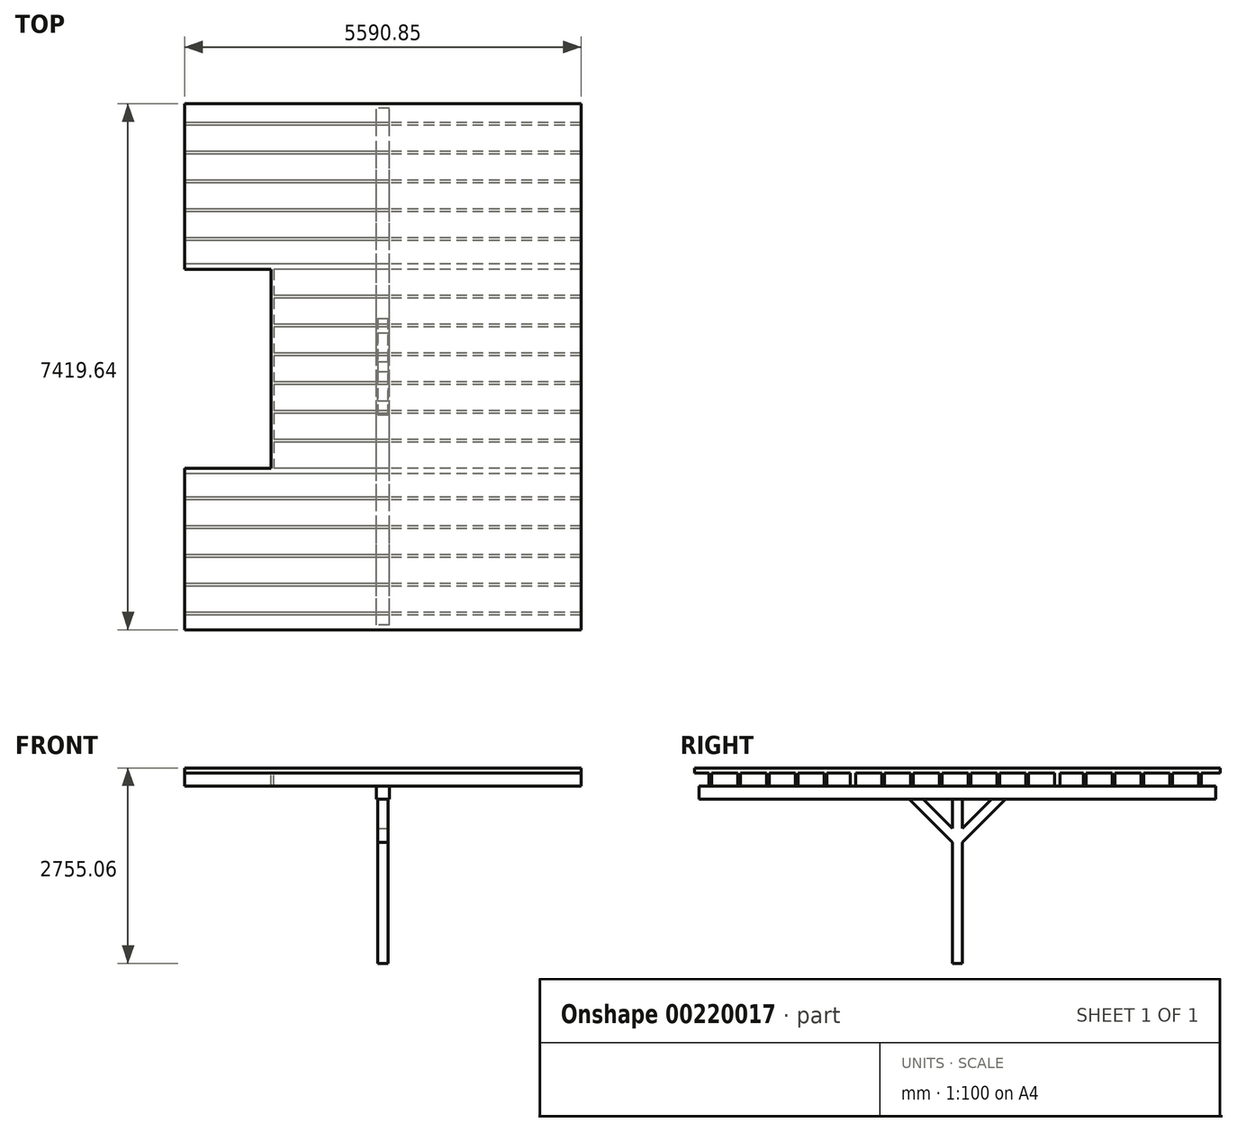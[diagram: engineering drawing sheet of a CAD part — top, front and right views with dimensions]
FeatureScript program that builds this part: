
annotation { "Feature Type Name" : "Feature", "Feature Type Description" : "" }
export const myFeature = defineFeature(function(context is Context, id is Id, definition is map)
    precondition{}
    {
        {
            var Q0;
            Q0=qCreatedBy(makeId("Top.planeOp"),FACE);
            var sketch = newSketch(context, id + "F0", { "sketchPlane" : qUnion([Q0])});
            skLineSegment(sketch, "E0.bottom", {"start": v(-4.2, 0) * mm, "end": v(5863.2, 0) * mm});
            skLineSegment(sketch, "E0.top", {"start": v(-4.2, -7696.2) * mm, "end": v(5863.2, -7696.2) * mm});
            skLineSegment(sketch, "E0.left", {"start": v(-4.2, 0) * mm, "end": v(-4.2, -7696.2) * mm});
            skLineSegment(sketch, "E0.right", {"start": v(5863.2, 0) * mm, "end": v(5863.2, -7696.2) * mm});
            skSolve(sketch);
        }
        {
            var Q0;
            Q0=makeQuery(id+"F0.imprint","IMPRINT",FACE,{"disambiguationData":[TD([[makeQuery(id+"F0.imprint","IMPRINT",EDGE,{"derivedFrom":sQuery(id+"F0.wireOp",EDGE,"E0.bottom")}),-1.0]])]});
            extrude(context, id + "F1", {"entities" : qUnion([Q0]), "depth" : 69.14 * mm});
        }
        {
            var Q0;
            Q0=makeQuery(id+"F1.opExtrude","CAP_FACE",FACE,{"disambiguationData":[OSD([sQuery(id+"F0.wireOp",EDGE,"E0.bottom"),sQuery(id+"F0.wireOp",EDGE,"E0.top"),sQuery(id+"F0.wireOp",EDGE,"E0.left"),sQuery(id+"F0.wireOp",EDGE,"E0.right")])],"isStart":true});
            var sketch = newSketch(context, id + "F2", { "sketchPlane" : qUnion([Q0])});
            skLineSegment(sketch, "E1.0", {"start": v(33.9, 7658.1) * mm, "end": v(5825.1, 7658.1) * mm});
            skLineSegment(sketch, "E1.1", {"start": v(33.9, 38.1) * mm, "end": v(33.9, 7658.1) * mm});
            skLineSegment(sketch, "E1.2", {"start": v(33.9, 38.1) * mm, "end": v(5825.1, 38.1) * mm});
            skLineSegment(sketch, "E1.3", {"start": v(5825.1, 38.1) * mm, "end": v(5825.1, 7658.1) * mm});
            skSolve(sketch);
        }
        {
            var Q0;
            Q0=makeQuery(id+"F2.imprint","IMPRINT",FACE,{"disambiguationData":[TD([[makeQuery(id+"F2.imprint","IMPRINT",EDGE,{"derivedFrom":sQuery(id+"F2.wireOp",EDGE,"E1.0")}),1.0]])]});
            extrude(context, id + "F3", {"entities" : qUnion([Q0]), "operationType" : NewBodyOperationType.ADD, "depth" : 184.15 * mm});
        }
        {
            var Q0;
            Q0=qCreatedBy(makeId("Right.planeOp"),FACE);
            var sketch = newSketch(context, id + "F4", { "sketchPlane" : qUnion([Q0])});
            skLineSegment(sketch, "E2.bottom", {"start": v(-406.4, 0) * mm, "end": v(-444.5, 0) * mm});
            skLineSegment(sketch, "E2.top", {"start": v(-406.4, -184.15) * mm, "end": v(-444.5, -184.15) * mm});
            skLineSegment(sketch, "E2.left", {"start": v(-406.4, 0) * mm, "end": v(-406.4, -184.15) * mm});
            skLineSegment(sketch, "E2.right", {"start": v(-444.5, 0) * mm, "end": v(-444.5, -184.15) * mm});
            skLineSegment(sketch, "E3.1.0.0", {"start": v(-812.8, 0) * mm, "end": v(-812.8, -184.15) * mm});
            skLineSegment(sketch, "E3.1.0.1", {"start": v(-850.9, 0) * mm, "end": v(-850.9, -184.15) * mm});
            skLineSegment(sketch, "E3.1.0.2", {"start": v(-812.8, 0) * mm, "end": v(-850.9, 0) * mm});
            skLineSegment(sketch, "E3.1.0.3", {"start": v(-812.8, -184.15) * mm, "end": v(-850.9, -184.15) * mm});
            skLineSegment(sketch, "E3.2.0.0", {"start": v(-1219.2, 0) * mm, "end": v(-1219.2, -184.15) * mm});
            skLineSegment(sketch, "E3.2.0.1", {"start": v(-1257.3, 0) * mm, "end": v(-1257.3, -184.15) * mm});
            skLineSegment(sketch, "E3.2.0.2", {"start": v(-1219.2, 0) * mm, "end": v(-1257.3, 0) * mm});
            skLineSegment(sketch, "E3.2.0.3", {"start": v(-1219.2, -184.15) * mm, "end": v(-1257.3, -184.15) * mm});
            skLineSegment(sketch, "E3.3.0.0", {"start": v(-1625.6, 0) * mm, "end": v(-1625.6, -184.15) * mm});
            skLineSegment(sketch, "E3.3.0.1", {"start": v(-1663.7, 0) * mm, "end": v(-1663.7, -184.15) * mm});
            skLineSegment(sketch, "E3.3.0.2", {"start": v(-1625.6, 0) * mm, "end": v(-1663.7, 0) * mm});
            skLineSegment(sketch, "E3.3.0.3", {"start": v(-1625.6, -184.15) * mm, "end": v(-1663.7, -184.15) * mm});
            skLineSegment(sketch, "E3.4.0.0", {"start": v(-2032, 0) * mm, "end": v(-2032, -184.15) * mm});
            skLineSegment(sketch, "E3.4.0.1", {"start": v(-2070.1, 0) * mm, "end": v(-2070.1, -184.15) * mm});
            skLineSegment(sketch, "E3.4.0.2", {"start": v(-2032, 0) * mm, "end": v(-2070.1, 0) * mm});
            skLineSegment(sketch, "E3.4.0.3", {"start": v(-2032, -184.15) * mm, "end": v(-2070.1, -184.15) * mm});
            skLineSegment(sketch, "E3.5.0.0", {"start": v(-2438.4, 0) * mm, "end": v(-2438.4, -184.15) * mm});
            skLineSegment(sketch, "E3.5.0.1", {"start": v(-2476.5, 0) * mm, "end": v(-2476.5, -184.15) * mm});
            skLineSegment(sketch, "E3.5.0.2", {"start": v(-2438.4, 0) * mm, "end": v(-2476.5, 0) * mm});
            skLineSegment(sketch, "E3.5.0.3", {"start": v(-2438.4, -184.15) * mm, "end": v(-2476.5, -184.15) * mm});
            skLineSegment(sketch, "E3.6.0.0", {"start": v(-2844.8, 0) * mm, "end": v(-2844.8, -184.15) * mm});
            skLineSegment(sketch, "E3.6.0.1", {"start": v(-2882.9, 0) * mm, "end": v(-2882.9, -184.15) * mm});
            skLineSegment(sketch, "E3.6.0.2", {"start": v(-2844.8, 0) * mm, "end": v(-2882.9, 0) * mm});
            skLineSegment(sketch, "E3.6.0.3", {"start": v(-2844.8, -184.15) * mm, "end": v(-2882.9, -184.15) * mm});
            skLineSegment(sketch, "E3.7.0.0", {"start": v(-3251.2, 0) * mm, "end": v(-3251.2, -184.15) * mm});
            skLineSegment(sketch, "E3.7.0.1", {"start": v(-3289.3, 0) * mm, "end": v(-3289.3, -184.15) * mm});
            skLineSegment(sketch, "E3.7.0.2", {"start": v(-3251.2, 0) * mm, "end": v(-3289.3, 0) * mm});
            skLineSegment(sketch, "E3.7.0.3", {"start": v(-3251.2, -184.15) * mm, "end": v(-3289.3, -184.15) * mm});
            skLineSegment(sketch, "E3.8.0.0", {"start": v(-3657.6, 0) * mm, "end": v(-3657.6, -184.15) * mm});
            skLineSegment(sketch, "E3.8.0.1", {"start": v(-3695.7, 0) * mm, "end": v(-3695.7, -184.15) * mm});
            skLineSegment(sketch, "E3.8.0.2", {"start": v(-3657.6, 0) * mm, "end": v(-3695.7, 0) * mm});
            skLineSegment(sketch, "E3.8.0.3", {"start": v(-3657.6, -184.15) * mm, "end": v(-3695.7, -184.15) * mm});
            skLineSegment(sketch, "E3.9.0.0", {"start": v(-4064, 0) * mm, "end": v(-4064, -184.15) * mm});
            skLineSegment(sketch, "E3.9.0.1", {"start": v(-4102.1, 0) * mm, "end": v(-4102.1, -184.15) * mm});
            skLineSegment(sketch, "E3.9.0.2", {"start": v(-4064, 0) * mm, "end": v(-4102.1, 0) * mm});
            skLineSegment(sketch, "E3.9.0.3", {"start": v(-4064, -184.15) * mm, "end": v(-4102.1, -184.15) * mm});
            skLineSegment(sketch, "E3.10.0.0", {"start": v(-4470.4, 0) * mm, "end": v(-4470.4, -184.15) * mm});
            skLineSegment(sketch, "E3.10.0.1", {"start": v(-4508.5, 0) * mm, "end": v(-4508.5, -184.15) * mm});
            skLineSegment(sketch, "E3.10.0.2", {"start": v(-4470.4, 0) * mm, "end": v(-4508.5, 0) * mm});
            skLineSegment(sketch, "E3.10.0.3", {"start": v(-4470.4, -184.15) * mm, "end": v(-4508.5, -184.15) * mm});
            skLineSegment(sketch, "E3.11.0.0", {"start": v(-4876.8, 0) * mm, "end": v(-4876.8, -184.15) * mm});
            skLineSegment(sketch, "E3.11.0.1", {"start": v(-4914.9, 0) * mm, "end": v(-4914.9, -184.15) * mm});
            skLineSegment(sketch, "E3.11.0.2", {"start": v(-4876.8, 0) * mm, "end": v(-4914.9, 0) * mm});
            skLineSegment(sketch, "E3.11.0.3", {"start": v(-4876.8, -184.15) * mm, "end": v(-4914.9, -184.15) * mm});
            skLineSegment(sketch, "E3.12.0.0", {"start": v(-5283.2, 0) * mm, "end": v(-5283.2, -184.15) * mm});
            skLineSegment(sketch, "E3.12.0.1", {"start": v(-5321.3, 0) * mm, "end": v(-5321.3, -184.15) * mm});
            skLineSegment(sketch, "E3.12.0.2", {"start": v(-5283.2, 0) * mm, "end": v(-5321.3, 0) * mm});
            skLineSegment(sketch, "E3.12.0.3", {"start": v(-5283.2, -184.15) * mm, "end": v(-5321.3, -184.15) * mm});
            skLineSegment(sketch, "E3.13.0.0", {"start": v(-5689.6, 0) * mm, "end": v(-5689.6, -184.15) * mm});
            skLineSegment(sketch, "E3.13.0.1", {"start": v(-5727.7, 0) * mm, "end": v(-5727.7, -184.15) * mm});
            skLineSegment(sketch, "E3.13.0.2", {"start": v(-5689.6, 0) * mm, "end": v(-5727.7, 0) * mm});
            skLineSegment(sketch, "E3.13.0.3", {"start": v(-5689.6, -184.15) * mm, "end": v(-5727.7, -184.15) * mm});
            skLineSegment(sketch, "E3.14.0.0", {"start": v(-6096, 0) * mm, "end": v(-6096, -184.15) * mm});
            skLineSegment(sketch, "E3.14.0.1", {"start": v(-6134.1, 0) * mm, "end": v(-6134.1, -184.15) * mm});
            skLineSegment(sketch, "E3.14.0.2", {"start": v(-6096, 0) * mm, "end": v(-6134.1, 0) * mm});
            skLineSegment(sketch, "E3.14.0.3", {"start": v(-6096, -184.15) * mm, "end": v(-6134.1, -184.15) * mm});
            skLineSegment(sketch, "E3.15.0.0", {"start": v(-6502.4, 0) * mm, "end": v(-6502.4, -184.15) * mm});
            skLineSegment(sketch, "E3.15.0.1", {"start": v(-6540.5, 0) * mm, "end": v(-6540.5, -184.15) * mm});
            skLineSegment(sketch, "E3.15.0.2", {"start": v(-6502.4, 0) * mm, "end": v(-6540.5, 0) * mm});
            skLineSegment(sketch, "E3.15.0.3", {"start": v(-6502.4, -184.15) * mm, "end": v(-6540.5, -184.15) * mm});
            skLineSegment(sketch, "E3.16.0.0", {"start": v(-6908.8, 0) * mm, "end": v(-6908.8, -184.15) * mm});
            skLineSegment(sketch, "E3.16.0.1", {"start": v(-6946.9, 0) * mm, "end": v(-6946.9, -184.15) * mm});
            skLineSegment(sketch, "E3.16.0.2", {"start": v(-6908.8, 0) * mm, "end": v(-6946.9, 0) * mm});
            skLineSegment(sketch, "E3.16.0.3", {"start": v(-6908.8, -184.15) * mm, "end": v(-6946.9, -184.15) * mm});
            skLineSegment(sketch, "E3.direction1", {"start": v(-444.5, -184.15) * mm, "end": v(-850.9, -184.15) * mm, "construction": true});
            skLineSegment(sketch, "E4.0.17.0", {"start": v(-7315.2, 0) * mm, "end": v(-7315.2, -184.15) * mm});
            skLineSegment(sketch, "E4.3.17.0", {"start": v(-7353.3, 0) * mm, "end": v(-7353.3, -184.15) * mm});
            skLineSegment(sketch, "E4.6.17.0", {"start": v(-7315.2, 0) * mm, "end": v(-7353.3, 0) * mm});
            skLineSegment(sketch, "E4.9.17.0", {"start": v(-7315.2, -184.15) * mm, "end": v(-7353.3, -184.15) * mm});
            skSolve(sketch);
        }
        {
            var Q0;
            Q0=makeQuery(id+"F4.imprint","IMPRINT",FACE,{"disambiguationData":[TD([[makeQuery(id+"F4.imprint","IMPRINT",EDGE,{"derivedFrom":sQuery(id+"F4.wireOp",EDGE,"E2.bottom")}),1.0]])]});
            var Q1;
            Q1=makeQuery(id+"F4.imprint","IMPRINT",FACE,{"disambiguationData":[TD([[makeQuery(id+"F4.imprint","IMPRINT",EDGE,{"derivedFrom":sQuery(id+"F4.wireOp",EDGE,"E3.1.0.0")}),-1.0]])]});
            var Q2;
            Q2=makeQuery(id+"F4.imprint","IMPRINT",FACE,{"disambiguationData":[TD([[makeQuery(id+"F4.imprint","IMPRINT",EDGE,{"derivedFrom":sQuery(id+"F4.wireOp",EDGE,"E3.2.0.0")}),-1.0]])]});
            var Q3;
            Q3=makeQuery(id+"F4.imprint","IMPRINT",FACE,{"disambiguationData":[TD([[makeQuery(id+"F4.imprint","IMPRINT",EDGE,{"derivedFrom":sQuery(id+"F4.wireOp",EDGE,"E3.3.0.0")}),-1.0]])]});
            var Q4;
            Q4=makeQuery(id+"F4.imprint","IMPRINT",FACE,{"disambiguationData":[TD([[makeQuery(id+"F4.imprint","IMPRINT",EDGE,{"derivedFrom":sQuery(id+"F4.wireOp",EDGE,"E3.4.0.0")}),-1.0]])]});
            var Q5;
            Q5=makeQuery(id+"F4.imprint","IMPRINT",FACE,{"disambiguationData":[TD([[makeQuery(id+"F4.imprint","IMPRINT",EDGE,{"derivedFrom":sQuery(id+"F4.wireOp",EDGE,"E3.5.0.0")}),-1.0]])]});
            var Q6;
            Q6=makeQuery(id+"F4.imprint","IMPRINT",FACE,{"disambiguationData":[TD([[makeQuery(id+"F4.imprint","IMPRINT",EDGE,{"derivedFrom":sQuery(id+"F4.wireOp",EDGE,"E3.6.0.0")}),-1.0]])]});
            var Q7;
            Q7=makeQuery(id+"F4.imprint","IMPRINT",FACE,{"disambiguationData":[TD([[makeQuery(id+"F4.imprint","IMPRINT",EDGE,{"derivedFrom":sQuery(id+"F4.wireOp",EDGE,"E3.7.0.0")}),-1.0]])]});
            var Q8;
            Q8=makeQuery(id+"F4.imprint","IMPRINT",FACE,{"disambiguationData":[TD([[makeQuery(id+"F4.imprint","IMPRINT",EDGE,{"derivedFrom":sQuery(id+"F4.wireOp",EDGE,"E3.8.0.0")}),-1.0]])]});
            var Q9;
            Q9=makeQuery(id+"F4.imprint","IMPRINT",FACE,{"disambiguationData":[TD([[makeQuery(id+"F4.imprint","IMPRINT",EDGE,{"derivedFrom":sQuery(id+"F4.wireOp",EDGE,"E3.9.0.0")}),-1.0]])]});
            var Q10;
            Q10=makeQuery(id+"F4.imprint","IMPRINT",FACE,{"disambiguationData":[TD([[makeQuery(id+"F4.imprint","IMPRINT",EDGE,{"derivedFrom":sQuery(id+"F4.wireOp",EDGE,"E3.10.0.0")}),-1.0]])]});
            var Q11;
            Q11=makeQuery(id+"F4.imprint","IMPRINT",FACE,{"disambiguationData":[TD([[makeQuery(id+"F4.imprint","IMPRINT",EDGE,{"derivedFrom":sQuery(id+"F4.wireOp",EDGE,"E3.11.0.0")}),-1.0]])]});
            var Q12;
            Q12=makeQuery(id+"F4.imprint","IMPRINT",FACE,{"disambiguationData":[TD([[makeQuery(id+"F4.imprint","IMPRINT",EDGE,{"derivedFrom":sQuery(id+"F4.wireOp",EDGE,"E3.12.0.0")}),-1.0]])]});
            var Q13;
            Q13=makeQuery(id+"F4.imprint","IMPRINT",FACE,{"disambiguationData":[TD([[makeQuery(id+"F4.imprint","IMPRINT",EDGE,{"derivedFrom":sQuery(id+"F4.wireOp",EDGE,"E3.13.0.0")}),-1.0]])]});
            var Q14;
            Q14=makeQuery(id+"F4.imprint","IMPRINT",FACE,{"disambiguationData":[TD([[makeQuery(id+"F4.imprint","IMPRINT",EDGE,{"derivedFrom":sQuery(id+"F4.wireOp",EDGE,"E3.14.0.0")}),-1.0]])]});
            var Q15;
            Q15=makeQuery(id+"F4.imprint","IMPRINT",FACE,{"disambiguationData":[TD([[makeQuery(id+"F4.imprint","IMPRINT",EDGE,{"derivedFrom":sQuery(id+"F4.wireOp",EDGE,"E3.15.0.0")}),-1.0]])]});
            var Q16;
            Q16=makeQuery(id+"F4.imprint","IMPRINT",FACE,{"disambiguationData":[TD([[makeQuery(id+"F4.imprint","IMPRINT",EDGE,{"derivedFrom":sQuery(id+"F4.wireOp",EDGE,"E3.16.0.0")}),-1.0]])]});
            var Q17;
            Q17=makeQuery(id+"F4.imprint","IMPRINT",FACE,{"disambiguationData":[TD([[makeQuery(id+"F4.imprint","IMPRINT",EDGE,{"derivedFrom":sQuery(id+"F4.wireOp",EDGE,"E4.0.17.0")}),-1.0]])]});
            var Q18;
            Q18=makeQuery(id+"F1.opExtrude","SWEPT_FACE",FACE,{"disambiguationData":[OSD([sQuery(id+"F0.wireOp",EDGE,"E0.right")])]});
            extrude(context, id + "F5", {"entities" : qUnion([Q0, Q1, Q2, Q3, Q4, Q5, Q6, Q7, Q8, Q9, Q10, Q11, Q12, Q13, Q14, Q15, Q16, Q17]), "operationType" : NewBodyOperationType.ADD, "endBound" : BoundingType.UP_TO_SURFACE, "endBoundEntityFace" : qUnion([Q18]), "depth" : 25.4 * mm});
        }
        {
            var Q0;
            {var subQ0=sQuery(id+"F0.wireOp",EDGE,"E0.bottom");Q0=makeQuery(id+"F3.boolean.opBoolean","MERGE",FACE,{"derivedFrom":[makeQuery(id+"F1.opExtrude","SWEPT_FACE",FACE,{"disambiguationData":[OSD([subQ0])]}),makeQuery(id+"F3.opExtrude","SWEPT_FACE",FACE,{"disambiguationData":[OSD([subQ0])]})]});}
            cPlane(context, id + "F6", {"entities" : qUnion([Q0]), "cplaneType" : CPlaneType.OFFSET, "offset" : 203.2 * mm, "oppositeDirection" : true, "width" : 152.4 * mm, "height" : 152.4 * mm});
        }
        {
            var Q0;
            Q0=qCreatedBy(id+"F6.planeOp",FACE);
            var sketch = newSketch(context, id + "F7", { "sketchPlane" : qUnion([Q0])});
            skLineSegment(sketch, "E5.bottom", {"start": v(-3021.58, -184.15) * mm, "end": v(-2837.43, -184.15) * mm});
            skLineSegment(sketch, "E5.top", {"start": v(-3021.58, -368.3) * mm, "end": v(-2837.43, -368.3) * mm});
            skLineSegment(sketch, "E5.left", {"start": v(-3021.58, -184.15) * mm, "end": v(-3021.58, -368.3) * mm});
            skLineSegment(sketch, "E5.right", {"start": v(-2837.43, -184.15) * mm, "end": v(-2837.43, -368.3) * mm});
            skSolve(sketch);
        }
        {
            var Q0;
            Q0=makeQuery(id+"F7.imprint","IMPRINT",FACE,{"disambiguationData":[TD([[makeQuery(id+"F7.imprint","IMPRINT",EDGE,{"derivedFrom":sQuery(id+"F7.wireOp",EDGE,"E5.bottom")}),-1.0]])]});
            extrude(context, id + "F8", {"entities" : qUnion([Q0]), "operationType" : NewBodyOperationType.ADD, "oppositeDirection" : true, "depth" : 7289.8 * mm});
        }
        {
            var Q0;
            Q0=makeQuery(id+"F8.opExtrude","SWEPT_FACE",FACE,{"disambiguationData":[OSD([sQuery(id+"F7.wireOp",EDGE,"E5.top")])]});
            var sketch = newSketch(context, id + "F9", { "sketchPlane" : qUnion([Q0])});
            skLineSegment(sketch, "E6", {"start": v(2929.5, 7493) * mm, "end": v(2929.5, 203.2) * mm, "construction": true});
            skLineSegment(sketch, "E7", {"start": v(2837.43, 3848.1) * mm, "end": v(3021.58, 3848.1) * mm, "construction": true});
            skLineSegment(sketch, "E8.bottom", {"start": v(2999.36, 3778.25) * mm, "end": v(2859.66, 3778.25) * mm});
            skLineSegment(sketch, "E8.top", {"start": v(2999.36, 3917.95) * mm, "end": v(2859.66, 3917.95) * mm});
            skLineSegment(sketch, "E8.left", {"start": v(2999.36, 3778.25) * mm, "end": v(2999.36, 3917.95) * mm});
            skLineSegment(sketch, "E8.right", {"start": v(2859.66, 3778.25) * mm, "end": v(2859.66, 3917.95) * mm});
            skPoint(sketch, "E8.middle", {"position": v(2929.5, 3848.1) * mm});
            skSolve(sketch);
        }
        {
            var Q0;
            Q0=makeQuery(id+"F9.imprint","IMPRINT",FACE,{"disambiguationData":[TD([[makeQuery(id+"F9.imprint","IMPRINT",EDGE,{"derivedFrom":sQuery(id+"F9.wireOp",EDGE,"E8.bottom")}),-1.0]])]});
            extrude(context, id + "F10", {"entities" : qUnion([Q0]), "operationType" : NewBodyOperationType.ADD, "depth" : 2317.62 * mm});
        }
        {
            var Q0;
            Q0=makeQuery(id+"F10.opExtrude","SWEPT_FACE",FACE,{"disambiguationData":[OSD([sQuery(id+"F9.wireOp",EDGE,"E8.left")])]});
            var sketch = newSketch(context, id + "F11", { "sketchPlane" : qUnion([Q0])});
            skLineSegment(sketch, "E9", {"start": v(-4329.98, -368.3) * mm, "end": v(-3917.95, -780.33) * mm});
            skLineSegment(sketch, "E10", {"start": v(-3917.95, -780.33) * mm, "end": v(-3917.95, -977.9) * mm});
            skLineSegment(sketch, "E11", {"start": v(-3917.95, -977.9) * mm, "end": v(-4527.55, -368.3) * mm});
            skLineSegment(sketch, "E12", {"start": v(-4527.55, -368.3) * mm, "end": v(-4329.98, -368.3) * mm});
            skLineSegment(sketch, "E13", {"start": v(-3848.1, -1904.76) * mm, "end": v(-3848.1, -2685.92) * mm, "construction": true});
            skLineSegment(sketch, "E14.MirrorCS", {"start": v(-3168.65, -368.3) * mm, "end": v(-3366.22, -368.3) * mm});
            skLineSegment(sketch, "E15.MirrorCS", {"start": v(-3778.25, -977.9) * mm, "end": v(-3168.65, -368.3) * mm});
            skLineSegment(sketch, "E16.MirrorCS", {"start": v(-3366.22, -368.3) * mm, "end": v(-3778.25, -780.33) * mm});
            skLineSegment(sketch, "E17.MirrorCS", {"start": v(-3778.25, -780.33) * mm, "end": v(-3778.25, -977.9) * mm});
            skSolve(sketch);
        }
        {
            var Q0;
            Q0=makeQuery(id+"F11.imprint","IMPRINT",FACE,{"disambiguationData":[TD([[makeQuery(id+"F11.imprint","IMPRINT",EDGE,{"derivedFrom":sQuery(id+"F11.wireOp",EDGE,"E9")}),-1.0]])]});
            var Q1;
            Q1=makeQuery(id+"F11.imprint","IMPRINT",FACE,{"disambiguationData":[TD([[makeQuery(id+"F11.imprint","IMPRINT",EDGE,{"derivedFrom":sQuery(id+"F11.wireOp",EDGE,"E14.MirrorCS")}),1.0]])]});
            var Q2;
            Q2=makeQuery(id+"F11.imprint","IMPRINT",FACE,{"disambiguationData":[TD([[makeQuery(id+"F11.imprint","IMPRINT",EDGE,{"derivedFrom":sQuery(id+"F11.wireOp",EDGE,"E14.MirrorCS")}),-1.0]])]});
            var Q3;
            Q3=makeQuery(id+"F10.opExtrude","SWEPT_FACE",FACE,{"disambiguationData":[OSD([sQuery(id+"F9.wireOp",EDGE,"E8.right")])]});
            extrude(context, id + "F12", {"entities" : qUnion([Q0, Q1, Q2]), "operationType" : NewBodyOperationType.ADD, "endBound" : BoundingType.UP_TO_SURFACE, "oppositeDirection" : true, "endBoundEntityFace" : qUnion([Q3]), "depth" : 25.4 * mm});
        }
        {
            var Q0;
            Q0=makeQuery(id+"F1.opExtrude","CAP_FACE",FACE,{"disambiguationData":[OSD([sQuery(id+"F0.wireOp",EDGE,"E0.bottom"),sQuery(id+"F0.wireOp",EDGE,"E0.top"),sQuery(id+"F0.wireOp",EDGE,"E0.left"),sQuery(id+"F0.wireOp",EDGE,"E0.right")])],"isStart":false});
            var sketch = newSketch(context, id + "F13", { "sketchPlane" : qUnion([Q0])});
            skLineSegment(sketch, "E18.0", {"start": v(134.08, -138.28) * mm, "end": v(5724.93, -138.28) * mm});
            skLineSegment(sketch, "E18.1", {"start": v(134.08, -138.28) * mm, "end": v(134.08, -7557.92) * mm});
            skLineSegment(sketch, "E18.2", {"start": v(134.08, -7557.92) * mm, "end": v(5724.93, -7557.92) * mm});
            skLineSegment(sketch, "E18.3", {"start": v(5724.93, -138.28) * mm, "end": v(5724.93, -7557.92) * mm});
            skLineSegment(sketch, "E19.0", {"start": v(-4.2, 0) * mm, "end": v(5863.2, 0) * mm});
            skLineSegment(sketch, "E20.0", {"start": v(-4.2, 0) * mm, "end": v(-4.2, -7696.2) * mm});
            skLineSegment(sketch, "E21.0", {"start": v(-4.2, -7696.2) * mm, "end": v(5863.2, -7696.2) * mm});
            skLineSegment(sketch, "E22.0", {"start": v(5863.2, 0) * mm, "end": v(5863.2, -7696.2) * mm});
            skSolve(sketch);
        }
        {
            var Q0;
            Q0=makeQuery(id+"F13.imprint","IMPRINT",FACE,{"disambiguationData":[TD([[makeQuery(id+"F13.imprint","IMPRINT",EDGE,{"derivedFrom":sQuery(id+"F13.wireOp",EDGE,"E18.0")}),1.0]])]});
            var Q1;
            Q1=makeQuery(id+"F5.boolean.opBoolean","MERGE",FACE,{"derivedFrom":[makeQuery(id+"F3.opExtrude","CAP_FACE",FACE,{"disambiguationData":[OSD([sQuery(id+"F0.wireOp",EDGE,"E0.bottom"),sQuery(id+"F0.wireOp",EDGE,"E0.top"),sQuery(id+"F0.wireOp",EDGE,"E0.left"),sQuery(id+"F0.wireOp",EDGE,"E0.right"),sQuery(id+"F2.wireOp",EDGE,"E1.0"),sQuery(id+"F2.wireOp",EDGE,"E1.1"),sQuery(id+"F2.wireOp",EDGE,"E1.2"),sQuery(id+"F2.wireOp",EDGE,"E1.3")])],"isStart":false}),makeQuery(id+"F5.opExtrude","SWEPT_FACE",FACE,{"disambiguationData":[OSD([sQuery(id+"F4.wireOp",EDGE,"E2.top")])]}),makeQuery(id+"F5.opExtrude","SWEPT_FACE",FACE,{"disambiguationData":[OSD([sQuery(id+"F4.wireOp",EDGE,"E3.1.0.3")])]}),makeQuery(id+"F5.opExtrude","SWEPT_FACE",FACE,{"disambiguationData":[OSD([sQuery(id+"F4.wireOp",EDGE,"E3.2.0.3")])]}),makeQuery(id+"F5.opExtrude","SWEPT_FACE",FACE,{"disambiguationData":[OSD([sQuery(id+"F4.wireOp",EDGE,"E3.3.0.3")])]}),makeQuery(id+"F5.opExtrude","SWEPT_FACE",FACE,{"disambiguationData":[OSD([sQuery(id+"F4.wireOp",EDGE,"E3.4.0.3")])]}),makeQuery(id+"F5.opExtrude","SWEPT_FACE",FACE,{"disambiguationData":[OSD([sQuery(id+"F4.wireOp",EDGE,"E3.5.0.3")])]}),makeQuery(id+"F5.opExtrude","SWEPT_FACE",FACE,{"disambiguationData":[OSD([sQuery(id+"F4.wireOp",EDGE,"E3.6.0.3")])]}),makeQuery(id+"F5.opExtrude","SWEPT_FACE",FACE,{"disambiguationData":[OSD([sQuery(id+"F4.wireOp",EDGE,"E3.7.0.3")])]}),makeQuery(id+"F5.opExtrude","SWEPT_FACE",FACE,{"disambiguationData":[OSD([sQuery(id+"F4.wireOp",EDGE,"E3.8.0.3")])]}),makeQuery(id+"F5.opExtrude","SWEPT_FACE",FACE,{"disambiguationData":[OSD([sQuery(id+"F4.wireOp",EDGE,"E3.9.0.3")])]}),makeQuery(id+"F5.opExtrude","SWEPT_FACE",FACE,{"disambiguationData":[OSD([sQuery(id+"F4.wireOp",EDGE,"E3.10.0.3")])]}),makeQuery(id+"F5.opExtrude","SWEPT_FACE",FACE,{"disambiguationData":[OSD([sQuery(id+"F4.wireOp",EDGE,"E3.11.0.3")])]}),makeQuery(id+"F5.opExtrude","SWEPT_FACE",FACE,{"disambiguationData":[OSD([sQuery(id+"F4.wireOp",EDGE,"E3.12.0.3")])]}),makeQuery(id+"F5.opExtrude","SWEPT_FACE",FACE,{"disambiguationData":[OSD([sQuery(id+"F4.wireOp",EDGE,"E3.13.0.3")])]}),makeQuery(id+"F5.opExtrude","SWEPT_FACE",FACE,{"disambiguationData":[OSD([sQuery(id+"F4.wireOp",EDGE,"E3.14.0.3")])]}),makeQuery(id+"F5.opExtrude","SWEPT_FACE",FACE,{"disambiguationData":[OSD([sQuery(id+"F4.wireOp",EDGE,"E3.15.0.3")])]}),makeQuery(id+"F5.opExtrude","SWEPT_FACE",FACE,{"disambiguationData":[OSD([sQuery(id+"F4.wireOp",EDGE,"E3.16.0.3")])]}),makeQuery(id+"F5.opExtrude","SWEPT_FACE",FACE,{"disambiguationData":[OSD([sQuery(id+"F4.wireOp",EDGE,"E4.9.17.0")])]})]});
            extrude(context, id + "F14", {"entities" : qUnion([Q0]), "operationType" : NewBodyOperationType.REMOVE, "endBound" : BoundingType.UP_TO_SURFACE, "oppositeDirection" : true, "endBoundEntityFace" : qUnion([Q1]), "depth" : 25.4 * mm});
        }
        {
            var Q0;
            Q0=makeQuery(id+"F1.opExtrude","CAP_FACE",FACE,{"disambiguationData":[OSD([sQuery(id+"F0.wireOp",EDGE,"E0.bottom"),sQuery(id+"F0.wireOp",EDGE,"E0.top"),sQuery(id+"F0.wireOp",EDGE,"E0.left"),sQuery(id+"F0.wireOp",EDGE,"E0.right")])],"isStart":false});
            var sketch = newSketch(context, id + "F15", { "sketchPlane" : qUnion([Q0])});
            skLineSegment(sketch, "E23.bottom", {"start": v(134.08, -2476.5) * mm, "end": v(1353.28, -2476.5) * mm});
            skLineSegment(sketch, "E23.top", {"start": v(134.08, -5283.2) * mm, "end": v(1353.28, -5283.2) * mm});
            skLineSegment(sketch, "E23.left", {"start": v(134.08, -2476.5) * mm, "end": v(134.08, -5283.2) * mm});
            skLineSegment(sketch, "E23.right", {"start": v(1353.28, -2476.5) * mm, "end": v(1353.28, -5283.2) * mm});
            skSolve(sketch);
        }
        {
            var Q0;
            Q0=makeQuery(id+"F15.imprint","IMPRINT",FACE,{"disambiguationData":[TD([[makeQuery(id+"F15.imprint","IMPRINT",EDGE,{"derivedFrom":sQuery(id+"F15.wireOp",EDGE,"E23.bottom")}),-1.0]])]});
            var Q1;
            Q1=makeQuery(id+"F14.boolean.opBoolean","SPLIT",FACE,{"disambiguationData":[TD([makeQuery(id+"F5.opExtrude","SWEPT_FACE",FACE,{"disambiguationData":[OSD([sQuery(id+"F4.wireOp",EDGE,"E3.5.0.0")])]}),makeQuery(id+"F5.opExtrude","SWEPT_FACE",FACE,{"disambiguationData":[OSD([sQuery(id+"F4.wireOp",EDGE,"E3.5.0.1")])]}),makeQuery(id+"F8.opExtrude","SWEPT_FACE",FACE,{"disambiguationData":[OSD([sQuery(id+"F7.wireOp",EDGE,"E5.bottom")])]}),makeQuery(id+"F8.opExtrude","SWEPT_FACE",FACE,{"disambiguationData":[OSD([sQuery(id+"F7.wireOp",EDGE,"E5.right")])]}),makeQuery(id+"F14.opExtrude","SWEPT_FACE",FACE,{"disambiguationData":[OSD([sQuery(id+"F13.wireOp",EDGE,"E18.1")])]})])],"derivedFrom":makeQuery(id+"F5.boolean.opBoolean","MERGE",FACE,{"derivedFrom":[makeQuery(id+"F3.opExtrude","CAP_FACE",FACE,{"disambiguationData":[OSD([sQuery(id+"F0.wireOp",EDGE,"E0.bottom"),sQuery(id+"F0.wireOp",EDGE,"E0.top"),sQuery(id+"F0.wireOp",EDGE,"E0.left"),sQuery(id+"F0.wireOp",EDGE,"E0.right"),sQuery(id+"F2.wireOp",EDGE,"E1.0"),sQuery(id+"F2.wireOp",EDGE,"E1.1"),sQuery(id+"F2.wireOp",EDGE,"E1.2"),sQuery(id+"F2.wireOp",EDGE,"E1.3")])],"isStart":false}),makeQuery(id+"F5.opExtrude","SWEPT_FACE",FACE,{"disambiguationData":[OSD([sQuery(id+"F4.wireOp",EDGE,"E2.top")])]}),makeQuery(id+"F5.opExtrude","SWEPT_FACE",FACE,{"disambiguationData":[OSD([sQuery(id+"F4.wireOp",EDGE,"E3.1.0.3")])]}),makeQuery(id+"F5.opExtrude","SWEPT_FACE",FACE,{"disambiguationData":[OSD([sQuery(id+"F4.wireOp",EDGE,"E3.2.0.3")])]}),makeQuery(id+"F5.opExtrude","SWEPT_FACE",FACE,{"disambiguationData":[OSD([sQuery(id+"F4.wireOp",EDGE,"E3.3.0.3")])]}),makeQuery(id+"F5.opExtrude","SWEPT_FACE",FACE,{"disambiguationData":[OSD([sQuery(id+"F4.wireOp",EDGE,"E3.4.0.3")])]}),makeQuery(id+"F5.opExtrude","SWEPT_FACE",FACE,{"disambiguationData":[OSD([sQuery(id+"F4.wireOp",EDGE,"E3.5.0.3")])]}),makeQuery(id+"F5.opExtrude","SWEPT_FACE",FACE,{"disambiguationData":[OSD([sQuery(id+"F4.wireOp",EDGE,"E3.6.0.3")])]}),makeQuery(id+"F5.opExtrude","SWEPT_FACE",FACE,{"disambiguationData":[OSD([sQuery(id+"F4.wireOp",EDGE,"E3.7.0.3")])]}),makeQuery(id+"F5.opExtrude","SWEPT_FACE",FACE,{"disambiguationData":[OSD([sQuery(id+"F4.wireOp",EDGE,"E3.8.0.3")])]}),makeQuery(id+"F5.opExtrude","SWEPT_FACE",FACE,{"disambiguationData":[OSD([sQuery(id+"F4.wireOp",EDGE,"E3.9.0.3")])]}),makeQuery(id+"F5.opExtrude","SWEPT_FACE",FACE,{"disambiguationData":[OSD([sQuery(id+"F4.wireOp",EDGE,"E3.10.0.3")])]}),makeQuery(id+"F5.opExtrude","SWEPT_FACE",FACE,{"disambiguationData":[OSD([sQuery(id+"F4.wireOp",EDGE,"E3.11.0.3")])]}),makeQuery(id+"F5.opExtrude","SWEPT_FACE",FACE,{"disambiguationData":[OSD([sQuery(id+"F4.wireOp",EDGE,"E3.12.0.3")])]}),makeQuery(id+"F5.opExtrude","SWEPT_FACE",FACE,{"disambiguationData":[OSD([sQuery(id+"F4.wireOp",EDGE,"E3.13.0.3")])]}),makeQuery(id+"F5.opExtrude","SWEPT_FACE",FACE,{"disambiguationData":[OSD([sQuery(id+"F4.wireOp",EDGE,"E3.14.0.3")])]}),makeQuery(id+"F5.opExtrude","SWEPT_FACE",FACE,{"disambiguationData":[OSD([sQuery(id+"F4.wireOp",EDGE,"E3.15.0.3")])]}),makeQuery(id+"F5.opExtrude","SWEPT_FACE",FACE,{"disambiguationData":[OSD([sQuery(id+"F4.wireOp",EDGE,"E3.16.0.3")])]}),makeQuery(id+"F5.opExtrude","SWEPT_FACE",FACE,{"disambiguationData":[OSD([sQuery(id+"F4.wireOp",EDGE,"E4.9.17.0")])]})]})});
            extrude(context, id + "F16", {"entities" : qUnion([Q0]), "operationType" : NewBodyOperationType.REMOVE, "endBound" : BoundingType.UP_TO_SURFACE, "oppositeDirection" : true, "endBoundEntityFace" : qUnion([Q1]), "depth" : 25.4 * mm});
        }
        {
            var Q0;
            Q0=makeQuery(id+"F16.boolean.opBoolean","COPY",FACE,{"derivedFrom":makeQuery(id+"F16.opExtrude","SWEPT_FACE",FACE,{"disambiguationData":[OSD([sQuery(id+"F15.wireOp",EDGE,"E23.right")])]})});
            var sketch = newSketch(context, id + "F17", { "sketchPlane" : qUnion([Q0])});
            skLineSegment(sketch, "E24.bottom", {"start": v(2476.5, 69.14) * mm, "end": v(5283.2, 69.14) * mm});
            skLineSegment(sketch, "E24.top", {"start": v(2476.5, -184.15) * mm, "end": v(5283.2, -184.15) * mm});
            skLineSegment(sketch, "E24.left", {"start": v(2476.5, 69.14) * mm, "end": v(2476.5, -184.15) * mm});
            skLineSegment(sketch, "E24.right", {"start": v(5283.2, 69.14) * mm, "end": v(5283.2, -184.15) * mm});
            skSolve(sketch);
        }
        {
            var Q0;
            {var subQ1=makeQuery(id+"F16.opExtrude","SWEPT_FACE",FACE,{"disambiguationData":[OSD([sQuery(id+"F15.wireOp",EDGE,"E23.right")])]});var subQ2=makeQuery(id+"F5.opExtrude","SWEPT_FACE",FACE,{"disambiguationData":[OSD([sQuery(id+"F4.wireOp",EDGE,"E3.5.0.0")])]});var subQ3=makeQuery(id+"F16.boolean.opBoolean","INTERSECT",EDGE,{"derivedFrom":[subQ2,subQ1]});Q0=makeQuery(id+"F17.imprint","IMPRINT",FACE,{"disambiguationData":[TD([[makeQuery(id+"F17.imprint","IMPRINT",EDGE,{"derivedFrom":subQ3}),1.0]])]});}
            var Q1;
            {var subQ1=makeQuery(id+"F16.opExtrude","SWEPT_FACE",FACE,{"disambiguationData":[OSD([sQuery(id+"F15.wireOp",EDGE,"E23.right")])]});var subQ2=makeQuery(id+"F5.opExtrude","SWEPT_FACE",FACE,{"disambiguationData":[OSD([sQuery(id+"F4.wireOp",EDGE,"E3.5.0.1")])]});var subQ3=makeQuery(id+"F16.boolean.opBoolean","INTERSECT",EDGE,{"derivedFrom":[subQ2,subQ1]});Q1=makeQuery(id+"F17.imprint","IMPRINT",FACE,{"disambiguationData":[TD([[makeQuery(id+"F17.imprint","IMPRINT",EDGE,{"derivedFrom":subQ3}),-1.0]])]});}
            var Q2;
            {var subQ1=makeQuery(id+"F16.opExtrude","SWEPT_FACE",FACE,{"disambiguationData":[OSD([sQuery(id+"F15.wireOp",EDGE,"E23.right")])]});var subQ2=makeQuery(id+"F5.opExtrude","SWEPT_FACE",FACE,{"disambiguationData":[OSD([sQuery(id+"F4.wireOp",EDGE,"E3.6.0.1")])]});var subQ3=makeQuery(id+"F16.boolean.opBoolean","INTERSECT",EDGE,{"derivedFrom":[subQ2,subQ1]});Q2=makeQuery(id+"F17.imprint","IMPRINT",FACE,{"disambiguationData":[TD([[makeQuery(id+"F17.imprint","IMPRINT",EDGE,{"derivedFrom":subQ3}),-1.0]])]});}
            var Q3;
            {var subQ1=makeQuery(id+"F16.opExtrude","SWEPT_FACE",FACE,{"disambiguationData":[OSD([sQuery(id+"F15.wireOp",EDGE,"E23.right")])]});var subQ2=makeQuery(id+"F5.opExtrude","SWEPT_FACE",FACE,{"disambiguationData":[OSD([sQuery(id+"F4.wireOp",EDGE,"E3.7.0.1")])]});var subQ3=makeQuery(id+"F16.boolean.opBoolean","INTERSECT",EDGE,{"derivedFrom":[subQ2,subQ1]});Q3=makeQuery(id+"F17.imprint","IMPRINT",FACE,{"disambiguationData":[TD([[makeQuery(id+"F17.imprint","IMPRINT",EDGE,{"derivedFrom":subQ3}),-1.0]])]});}
            var Q4;
            {var subQ1=makeQuery(id+"F16.opExtrude","SWEPT_FACE",FACE,{"disambiguationData":[OSD([sQuery(id+"F15.wireOp",EDGE,"E23.right")])]});var subQ2=makeQuery(id+"F5.opExtrude","SWEPT_FACE",FACE,{"disambiguationData":[OSD([sQuery(id+"F4.wireOp",EDGE,"E3.8.0.1")])]});var subQ3=makeQuery(id+"F16.boolean.opBoolean","INTERSECT",EDGE,{"derivedFrom":[subQ2,subQ1]});Q4=makeQuery(id+"F17.imprint","IMPRINT",FACE,{"disambiguationData":[TD([[makeQuery(id+"F17.imprint","IMPRINT",EDGE,{"derivedFrom":subQ3}),-1.0]])]});}
            var Q5;
            {var subQ1=makeQuery(id+"F16.opExtrude","SWEPT_FACE",FACE,{"disambiguationData":[OSD([sQuery(id+"F15.wireOp",EDGE,"E23.right")])]});var subQ2=makeQuery(id+"F5.opExtrude","SWEPT_FACE",FACE,{"disambiguationData":[OSD([sQuery(id+"F4.wireOp",EDGE,"E3.9.0.1")])]});var subQ3=makeQuery(id+"F16.boolean.opBoolean","INTERSECT",EDGE,{"derivedFrom":[subQ2,subQ1]});Q5=makeQuery(id+"F17.imprint","IMPRINT",FACE,{"disambiguationData":[TD([[makeQuery(id+"F17.imprint","IMPRINT",EDGE,{"derivedFrom":subQ3}),-1.0]])]});}
            var Q6;
            {var subQ1=makeQuery(id+"F16.opExtrude","SWEPT_FACE",FACE,{"disambiguationData":[OSD([sQuery(id+"F15.wireOp",EDGE,"E23.right")])]});var subQ2=makeQuery(id+"F5.opExtrude","SWEPT_FACE",FACE,{"disambiguationData":[OSD([sQuery(id+"F4.wireOp",EDGE,"E3.10.0.1")])]});var subQ3=makeQuery(id+"F16.boolean.opBoolean","INTERSECT",EDGE,{"derivedFrom":[subQ2,subQ1]});Q6=makeQuery(id+"F17.imprint","IMPRINT",FACE,{"disambiguationData":[TD([[makeQuery(id+"F17.imprint","IMPRINT",EDGE,{"derivedFrom":subQ3}),-1.0]])]});}
            var Q7;
            {var subQ1=makeQuery(id+"F16.opExtrude","SWEPT_FACE",FACE,{"disambiguationData":[OSD([sQuery(id+"F15.wireOp",EDGE,"E23.right")])]});var subQ2=makeQuery(id+"F5.opExtrude","SWEPT_FACE",FACE,{"disambiguationData":[OSD([sQuery(id+"F4.wireOp",EDGE,"E3.11.0.1")])]});var subQ3=makeQuery(id+"F16.boolean.opBoolean","INTERSECT",EDGE,{"derivedFrom":[subQ2,subQ1]});Q7=makeQuery(id+"F17.imprint","IMPRINT",FACE,{"disambiguationData":[TD([[makeQuery(id+"F17.imprint","IMPRINT",EDGE,{"derivedFrom":subQ3}),-1.0]])]});}
            var Q8;
            {var subQ1=makeQuery(id+"F16.opExtrude","SWEPT_FACE",FACE,{"disambiguationData":[OSD([sQuery(id+"F15.wireOp",EDGE,"E23.right")])]});var subQ2=makeQuery(id+"F5.opExtrude","SWEPT_FACE",FACE,{"disambiguationData":[OSD([sQuery(id+"F4.wireOp",EDGE,"E3.6.0.0")])]});var subQ3=makeQuery(id+"F16.boolean.opBoolean","INTERSECT",EDGE,{"derivedFrom":[subQ2,subQ1]});Q8=makeQuery(id+"F17.imprint","IMPRINT",FACE,{"disambiguationData":[TD([[makeQuery(id+"F17.imprint","IMPRINT",EDGE,{"derivedFrom":subQ3}),1.0]])]});}
            extrude(context, id + "F18", {"entities" : qUnion([Q0, Q1, Q2, Q3, Q4, Q5, Q6, Q7, Q8]), "operationType" : NewBodyOperationType.ADD, "oppositeDirection" : true, "depth" : 38.1 * mm});
        }
        {
            var Q0;
            Q0=makeQuery(id+"F5.opExtrude","SWEPT_FACE",FACE,{"disambiguationData":[OSD([sQuery(id+"F4.wireOp",EDGE,"E3.12.0.1")])]});
            extrude(context, id + "F19", {"entities" : qUnion([Q0]), "operationType" : NewBodyOperationType.ADD, "depth" : 38.1 * mm});
        }
        {
            var Q0;
            Q0=makeQuery(id+"F5.opExtrude","SWEPT_FACE",FACE,{"disambiguationData":[OSD([sQuery(id+"F4.wireOp",EDGE,"E3.5.0.0")])]});
            extrude(context, id + "F20", {"entities" : qUnion([Q0]), "operationType" : NewBodyOperationType.ADD, "depth" : 38.1 * mm});
        }
    });
